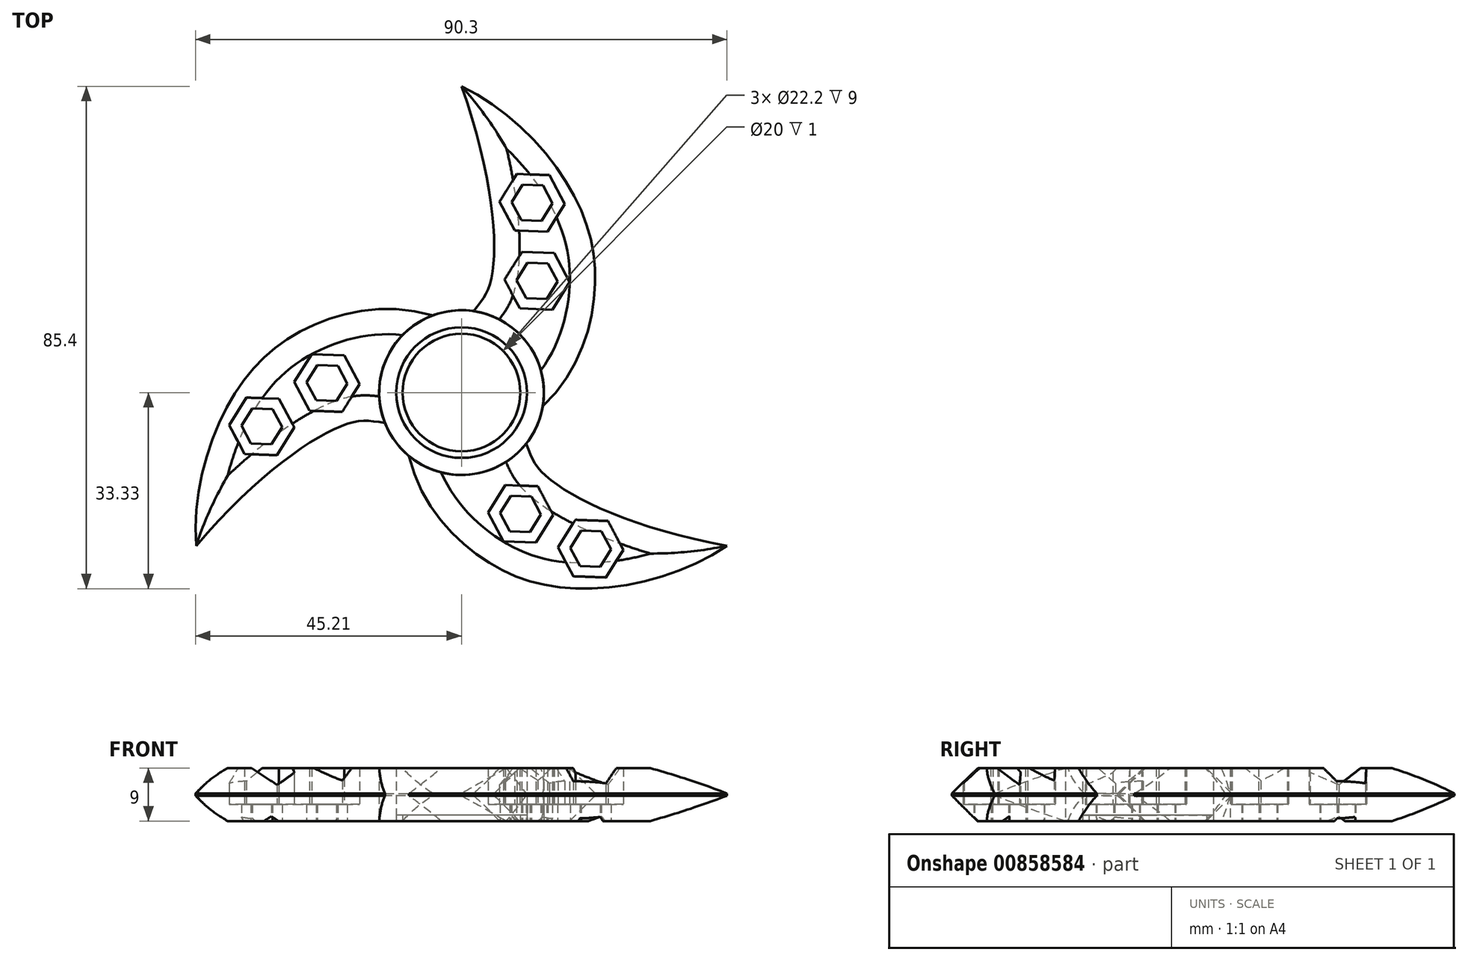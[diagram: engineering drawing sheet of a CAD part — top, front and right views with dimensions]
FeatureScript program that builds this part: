
annotation { "Feature Type Name" : "Feature", "Feature Type Description" : "" }
export const myFeature = defineFeature(function(context is Context, id is Id, definition is map)
    precondition{}
    {
        {
            var Q0;
            Q0=qCreatedBy(makeId("Top.planeOp"),FACE);
            var sketch = newSketch(context, id + "F0", { "sketchPlane" : qUnion([Q0])});
            skCircle(sketch, "E0", {"center": v(0, 0) * mm, "radius": 11.1 * mm});
            skLineSegment(sketch, "E1", {"start": v(0, 0) * mm, "end": v(0, 52.07) * mm, "construction": true});
            skLineSegment(sketch, "E2", {"start": v(0, 0) * mm, "end": v(63.41, -36.61) * mm, "construction": true});
            skFitSpline(sketch, "E3", {"points": [v(9.61, -5.55) * mm, v(22.5, 15.72) * mm, v(18.7, 34.28) * mm, v(0, 52.07) * mm], "startDerivative": vector(73.68, 46.4) * mm, "endDerivative": vector(-66.47, 31.25) * mm});
            skFitSpline(sketch, "E4", {"points": [v(0, 11.1) * mm, v(4.87, 18.55) * mm, v(0, 52.07) * mm], "startDerivative": vector(23.6, 34.07) * mm, "endDerivative": vector(-25.43, 71.66) * mm});
            skCircle(sketch, "E5", {"center": v(0, 0) * mm, "radius": 14 * mm});
            skCircle(sketch, "E6.cCircle", {"center": v(12, 32.27) * mm, "radius": 4.8 * mm, "construction": true});
            skLineSegment(sketch, "E6.0", {"start": v(17.54, 32.08) * mm, "end": v(14.6, 27.38) * mm});
            skLineSegment(sketch, "E6.1", {"start": v(14.6, 27.38) * mm, "end": v(9.06, 27.57) * mm});
            skLineSegment(sketch, "E6.2", {"start": v(9.06, 27.57) * mm, "end": v(6.46, 32.47) * mm});
            skLineSegment(sketch, "E6.3", {"start": v(6.46, 32.47) * mm, "end": v(9.4, 37.17) * mm});
            skLineSegment(sketch, "E6.4", {"start": v(9.4, 37.17) * mm, "end": v(14.94, 36.97) * mm});
            skLineSegment(sketch, "E6.5", {"start": v(14.94, 36.97) * mm, "end": v(17.54, 32.08) * mm});
            skPoint(sketch, "E6.0.midPoint", {"position": v(16.07, 29.73) * mm});
            skLineSegment(sketch, "E7.0.1.0", {"start": v(15.44, 14.1) * mm, "end": v(9.9, 14.3) * mm});
            skLineSegment(sketch, "E7.0.1.1", {"start": v(9.9, 14.3) * mm, "end": v(7.3, 19.2) * mm});
            skLineSegment(sketch, "E7.0.1.2", {"start": v(7.3, 19.2) * mm, "end": v(10.24, 23.9) * mm});
            skLineSegment(sketch, "E7.0.1.3", {"start": v(10.24, 23.9) * mm, "end": v(15.78, 23.7) * mm});
            skLineSegment(sketch, "E7.0.1.4", {"start": v(15.78, 23.7) * mm, "end": v(18.38, 18.8) * mm});
            skLineSegment(sketch, "E7.0.1.5", {"start": v(18.38, 18.8) * mm, "end": v(15.44, 14.1) * mm});
            skLineSegment(sketch, "E7.direction1", {"start": v(9.06, 27.57) * mm, "end": v(34.06, 27.57) * mm, "construction": true});
            skLineSegment(sketch, "E7.direction2", {"start": v(9.06, 27.57) * mm, "end": v(9.9, 14.3) * mm, "construction": true});
            skCircle(sketch, "E8", {"center": v(0, 0) * mm, "radius": 10 * mm});
            skCircle(sketch, "E9.cCircle", {"center": v(12, 32.27) * mm, "radius": 3 * mm, "construction": true});
            skLineSegment(sketch, "E9.0", {"start": v(15.46, 32.15) * mm, "end": v(13.62, 29.21) * mm});
            skLineSegment(sketch, "E9.1", {"start": v(13.62, 29.21) * mm, "end": v(10.16, 29.34) * mm});
            skLineSegment(sketch, "E9.2", {"start": v(10.16, 29.34) * mm, "end": v(8.54, 32.4) * mm});
            skLineSegment(sketch, "E9.3", {"start": v(8.54, 32.4) * mm, "end": v(10.37, 35.33) * mm});
            skLineSegment(sketch, "E9.4", {"start": v(10.37, 35.33) * mm, "end": v(13.84, 35.2) * mm});
            skLineSegment(sketch, "E9.5", {"start": v(13.84, 35.2) * mm, "end": v(15.46, 32.15) * mm});
            skPoint(sketch, "E9.0.midPoint", {"position": v(14.54, 30.68) * mm});
            skLineSegment(sketch, "E10", {"start": v(10.24, 23.9) * mm, "end": v(15.44, 14.1) * mm, "construction": true});
            skLineSegment(sketch, "E11", {"start": v(15.78, 23.7) * mm, "end": v(9.9, 14.3) * mm, "construction": true});
            skCircle(sketch, "E12.cCircle", {"center": v(12.84, 19) * mm, "radius": 3 * mm, "construction": true});
            skLineSegment(sketch, "E12.0", {"start": v(16.3, 18.88) * mm, "end": v(14.46, 15.94) * mm});
            skLineSegment(sketch, "E12.1", {"start": v(14.46, 15.94) * mm, "end": v(11, 16.06) * mm});
            skLineSegment(sketch, "E12.2", {"start": v(11, 16.06) * mm, "end": v(9.38, 19.12) * mm});
            skLineSegment(sketch, "E12.3", {"start": v(9.38, 19.12) * mm, "end": v(11.22, 22.06) * mm});
            skLineSegment(sketch, "E12.4", {"start": v(11.22, 22.06) * mm, "end": v(14.68, 21.94) * mm});
            skLineSegment(sketch, "E12.5", {"start": v(14.68, 21.94) * mm, "end": v(16.3, 18.88) * mm});
            skPoint(sketch, "E12.0.midPoint", {"position": v(15.38, 17.4) * mm});
            skSolve(sketch);
        }
        {
            var Q0;
            Q0 = qSketchRegion(id + "F0", true);
            extrude(context, id + "F1", {"entities" : qUnion([Q0]), "depth" : 9 * mm, "offsetDistance" : 25 * mm});
        }
        {
            var Q0;
            {var subQ0=sQuery(id+"F0.wireOp",EDGE,"E0");var subQ1=makeQuery(id+"F0.imprint","INTERSECT",VERTEX,{"derivedFrom":[subQ0,sQuery(id+"F0.wireOp",EDGE,"E3")]});Q0=makeQuery(id+"F0.imprint","IMPRINT",FACE,{"disambiguationData":[TD([[makeQuery(id+"F0.imprint","IMPRINT",EDGE,{"disambiguationData":[TD([[subQ1,1.0]])],"derivedFrom":subQ0}),1.0]])]});}
            extrude(context, id + "F2", {"entities" : qUnion([Q0]), "depth" : 1 * mm, "offsetDistance" : 25 * mm});
        }
        {
            var Q0;
            Q0=makeQuery(id+"F0.imprint","IMPRINT",FACE,{"disambiguationData":[TD([[makeQuery(id+"F0.imprint","IMPRINT",EDGE,{"derivedFrom":sQuery(id+"F0.wireOp",EDGE,"E6.0")}),-1.0]])]});
            var Q1;
            Q1=makeQuery(id+"F0.imprint","IMPRINT",FACE,{"disambiguationData":[TD([[makeQuery(id+"F0.imprint","IMPRINT",EDGE,{"derivedFrom":sQuery(id+"F0.wireOp",EDGE,"E7.0.1.0")}),-1.0]])]});
            extrude(context, id + "F3", {"entities" : qUnion([Q0, Q1]), "operationType" : NewBodyOperationType.ADD, "depth" : 2.85 * mm, "offsetDistance" : 25 * mm});
        }
        {
            var Q0;
            Q0=qCreatedBy(makeId("Front.planeOp"),FACE);
            var sketch = newSketch(context, id + "F4", { "sketchPlane" : qUnion([Q0])});
            skLineSegment(sketch, "E13", {"start": v(0, 0) * mm, "end": v(0, 39.09) * mm, "construction": true});
            skSolve(sketch);
        }
        {
            var Q0;
            Q0=makeQuery(id+"F1.opExtrude","SWEPT_BODY",BODY,{"disambiguationData":[OSD([sQuery(id+"F0.wireOp",EDGE,"E0"),sQuery(id+"F0.wireOp",EDGE,"E3"),sQuery(id+"F0.wireOp",EDGE,"E4"),sQuery(id+"F0.wireOp",EDGE,"E5"),sQuery(id+"F0.wireOp",EDGE,"E6.0"),sQuery(id+"F0.wireOp",EDGE,"E6.1"),sQuery(id+"F0.wireOp",EDGE,"E6.2"),sQuery(id+"F0.wireOp",EDGE,"E6.3"),sQuery(id+"F0.wireOp",EDGE,"E6.4"),sQuery(id+"F0.wireOp",EDGE,"E6.5"),sQuery(id+"F0.wireOp",EDGE,"E7.0.1.0"),sQuery(id+"F0.wireOp",EDGE,"E7.0.1.1"),sQuery(id+"F0.wireOp",EDGE,"E7.0.1.2"),sQuery(id+"F0.wireOp",EDGE,"E7.0.1.3"),sQuery(id+"F0.wireOp",EDGE,"E7.0.1.4"),sQuery(id+"F0.wireOp",EDGE,"E7.0.1.5")])]});
            var Q1;
            Q1=sQuery(id+"F4.wireOp",EDGE,"E13");
            circularPattern(context, id + "F5", {"entities" : qUnion([Q0]), "axis" : qUnion([Q1]), "angle" : 360 * degree, "instanceCount" : 3, "equalSpace" : true});
        }
        {
            var Q0;
            Q0=makeQuery(id+"F5.opPattern","COPY",EDGE,{"derivedFrom":makeQuery(id+"F1.opExtrude","CAP_EDGE",EDGE,{"disambiguationData":[OSD([sQuery(id+"F0.wireOp",EDGE,"E4")])],"isStart":false}),"instanceName":"1"});
            var Q1;
            Q1=makeQuery(id+"F5.opPattern","COPY",EDGE,{"derivedFrom":makeQuery(id+"F1.opExtrude","CAP_EDGE",EDGE,{"disambiguationData":[OSD([sQuery(id+"F0.wireOp",EDGE,"E3")])],"isStart":false}),"instanceName":"1"});
            var Q2;
            Q2=makeQuery(id+"F5.opPattern","COPY",EDGE,{"derivedFrom":makeQuery(id+"F1.opExtrude","CAP_EDGE",EDGE,{"disambiguationData":[OSD([sQuery(id+"F0.wireOp",EDGE,"E4")])],"isStart":true}),"instanceName":"1"});
            var Q3;
            Q3=makeQuery(id+"F5.opPattern","COPY",EDGE,{"derivedFrom":makeQuery(id+"F1.opExtrude","CAP_EDGE",EDGE,{"disambiguationData":[OSD([sQuery(id+"F0.wireOp",EDGE,"E3")])],"isStart":true}),"instanceName":"1"});
            var Q4;
            Q4=makeQuery(id+"F5.opPattern","COPY",EDGE,{"derivedFrom":makeQuery(id+"F1.opExtrude","CAP_EDGE",EDGE,{"disambiguationData":[OSD([sQuery(id+"F0.wireOp",EDGE,"E3")])],"isStart":false}),"instanceName":"2"});
            var Q5;
            Q5=makeQuery(id+"F5.opPattern","COPY",EDGE,{"derivedFrom":makeQuery(id+"F1.opExtrude","CAP_EDGE",EDGE,{"disambiguationData":[OSD([sQuery(id+"F0.wireOp",EDGE,"E3")])],"isStart":true}),"instanceName":"2"});
            var Q6;
            Q6=makeQuery(id+"F5.opPattern","COPY",EDGE,{"derivedFrom":makeQuery(id+"F1.opExtrude","CAP_EDGE",EDGE,{"disambiguationData":[OSD([sQuery(id+"F0.wireOp",EDGE,"E4")])],"isStart":true}),"instanceName":"2"});
            var Q7;
            Q7=makeQuery(id+"F1.opExtrude","CAP_EDGE",EDGE,{"disambiguationData":[OSD([sQuery(id+"F0.wireOp",EDGE,"E3")])],"isStart":true});
            var Q8;
            Q8=makeQuery(id+"F1.opExtrude","CAP_EDGE",EDGE,{"disambiguationData":[OSD([sQuery(id+"F0.wireOp",EDGE,"E4")])],"isStart":true});
            var Q9;
            Q9=makeQuery(id+"F1.opExtrude","CAP_EDGE",EDGE,{"disambiguationData":[OSD([sQuery(id+"F0.wireOp",EDGE,"E3")])],"isStart":false});
            var Q10;
            Q10=makeQuery(id+"F1.opExtrude","CAP_EDGE",EDGE,{"disambiguationData":[OSD([sQuery(id+"F0.wireOp",EDGE,"E4")])],"isStart":false});
            var Q11;
            Q11=makeQuery(id+"F5.opPattern","COPY",EDGE,{"derivedFrom":makeQuery(id+"F1.opExtrude","CAP_EDGE",EDGE,{"disambiguationData":[OSD([sQuery(id+"F0.wireOp",EDGE,"E4")])],"isStart":false}),"instanceName":"2"});
            chamfer(context, id + "F6", {"entities" : qUnion([Q0, Q1, Q2, Q3, Q4, Q5, Q6, Q7, Q8, Q9, Q10, Q11]), "width" : 4.32 * mm, "tangentPropagation" : true});
        }
    });
